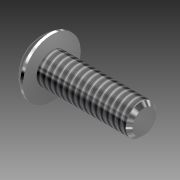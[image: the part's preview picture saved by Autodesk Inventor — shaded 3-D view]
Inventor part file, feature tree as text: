
AUTODESK INVENTOR PART (.ipt)
format: ipt  version: 2011 (Build 150239000, 239)  size: 118,272 bytes
history: native  units: in
note: dims shown in document units (in); Inventor stores cm internally (conversion verified against a paired STEP export)
features: other x1, imported_body x1, thread x1
ambient origin geometry x8: Origin, YZ Plane, XZ Plane, XY Plane, X Axis, Y Axis, Z Axis, Center Point
feature tree (3):
  parser-record x1  (decoder bookkeeping rows leaked as tree rows — omitted from the tree; the rows remain in map.json)
  imported_body  "Base1"
  thread  "Thread1"  [1 undecoded]
note: 1 required parameter value undecoded (feature->parameter linkage not recoverable at this tier; creation-order binding heuristic only, values carry confidence <= 0.55)
